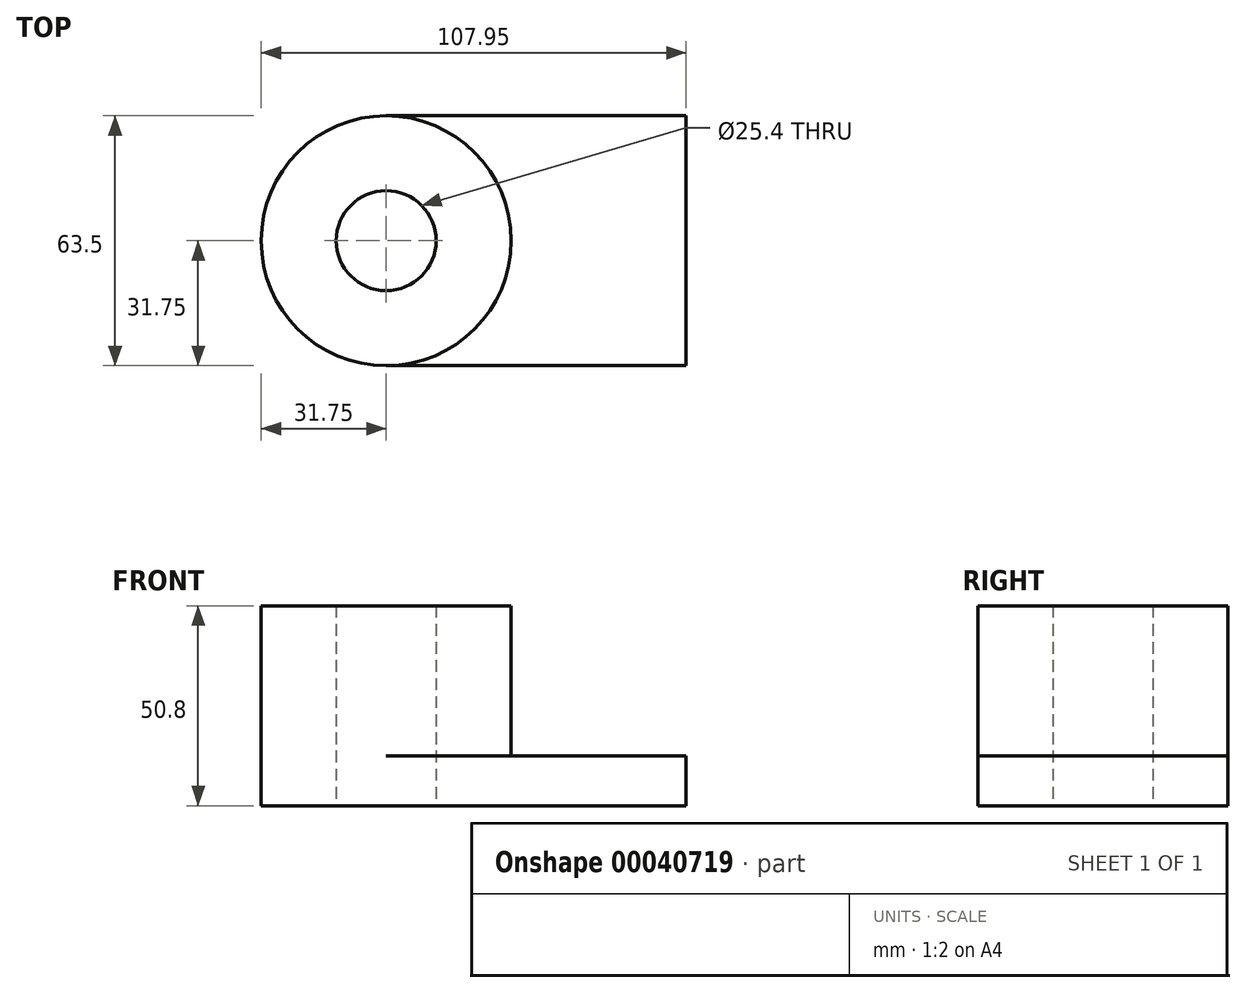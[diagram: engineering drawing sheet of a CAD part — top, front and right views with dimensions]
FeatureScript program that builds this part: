
annotation { "Feature Type Name" : "Feature", "Feature Type Description" : "" }
export const myFeature = defineFeature(function(context is Context, id is Id, definition is map)
    precondition{}
    {
        {
            var Q0;
            Q0=qCreatedBy(makeId("Top.planeOp"),FACE);
            var sketch = newSketch(context, id + "F0", { "sketchPlane" : qUnion([Q0])});
            skLineSegment(sketch, "E0.rect.bottom", {"start": v(38.1, 31.75) * mm, "end": v(-38.1, 31.75) * mm});
            skLineSegment(sketch, "E0.rect.top", {"start": v(38.1, -31.75) * mm, "end": v(-38.1, -31.75) * mm});
            skLineSegment(sketch, "E0.rect.left", {"start": v(38.1, 31.75) * mm, "end": v(38.1, -31.75) * mm});
            skLineSegment(sketch, "E0.rect.right", {"start": v(-38.1, 31.75) * mm, "end": v(-38.1, -31.75) * mm});
            skPoint(sketch, "E0.rect.middle", {"position": v(0, 0) * mm});
            skCircle(sketch, "E1", {"center": v(-38.1, 0) * mm, "radius": 12.7 * mm});
            skCircle(sketch, "E2", {"center": v(-38.1, 0) * mm, "radius": 31.75 * mm});
            skSolve(sketch);
        }
        {
            var Q0;
            Q0 = qSketchRegion(id + "F0", true);
            extrude(context, id + "F1", {"entities" : qUnion([Q0]), "depth" : 12.7 * mm});
        }
        {
            var Q0;
            {var subQ1=sQuery(id+"F0.wireOp",EDGE,"E0.rect.right");var subQ4=sQuery(id+"F0.wireOp",EDGE,"E1");var subQ6=makeQuery(id+"F0.imprint","INTERSECT",VERTEX,{"disambiguationData":[OD(0.0)],"derivedFrom":[subQ1,subQ4]});Q0=makeQuery(id+"F0.imprint","IMPRINT",FACE,{"disambiguationData":[TD([[makeQuery(id+"F0.imprint","IMPRINT",EDGE,{"disambiguationData":[TD([[subQ6,-1.0]])],"derivedFrom":subQ4}),-1.0]])]});}
            var Q1;
            {var subQ1=sQuery(id+"F0.wireOp",EDGE,"E0.rect.right");var subQ4=sQuery(id+"F0.wireOp",EDGE,"E1");var subQ6=makeQuery(id+"F0.imprint","INTERSECT",VERTEX,{"disambiguationData":[OD(0.0)],"derivedFrom":[subQ1,subQ4]});Q1=makeQuery(id+"F0.imprint","IMPRINT",FACE,{"disambiguationData":[TD([[makeQuery(id+"F0.imprint","IMPRINT",EDGE,{"disambiguationData":[TD([[subQ6,1.0]])],"derivedFrom":subQ4}),-1.0]])]});}
            extrude(context, id + "F2", {"entities" : qUnion([Q0, Q1]), "operationType" : NewBodyOperationType.ADD, "depth" : 50.8 * mm});
        }
    });
